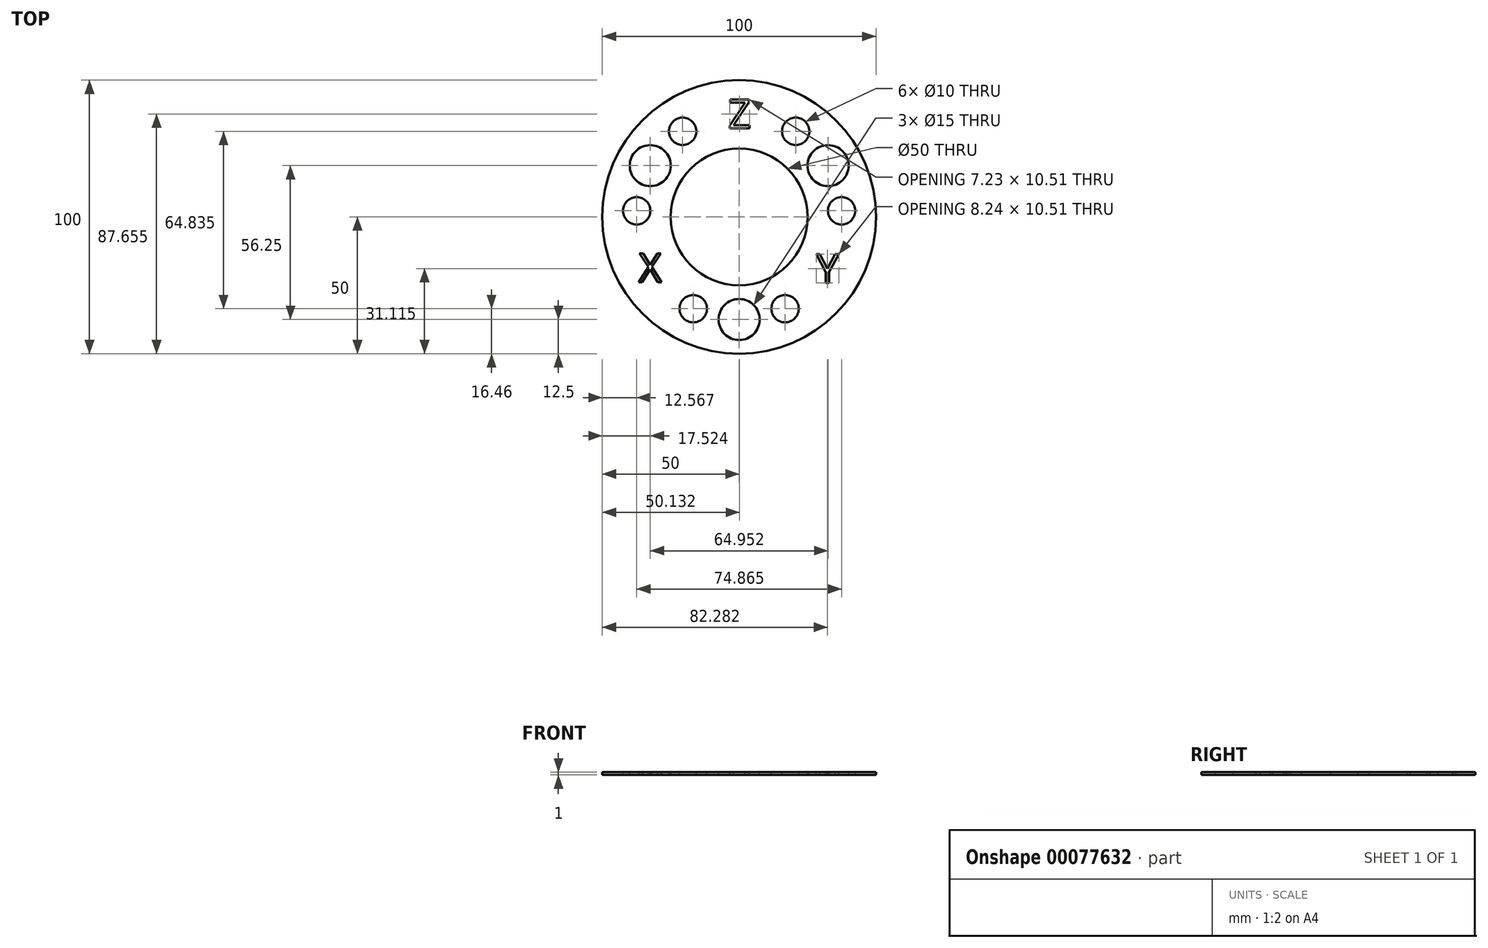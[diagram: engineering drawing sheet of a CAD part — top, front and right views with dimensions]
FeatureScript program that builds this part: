
annotation { "Feature Type Name" : "Feature", "Feature Type Description" : "" }
export const myFeature = defineFeature(function(context is Context, id is Id, definition is map)
    precondition{}
    {
        {
            var Q0;
            Q0=qCreatedBy(makeId("Top.planeOp"),FACE);
            var sketch = newSketch(context, id + "F0", { "sketchPlane" : qUnion([Q0])});
            skCircle(sketch, "E0", {"center": v(0, 0) * mm, "radius": 50 * mm});
            skCircle(sketch, "E1", {"center": v(0, 0) * mm, "radius": 25 * mm});
            skSolve(sketch);
        }
        {
            var Q0;
            Q0 = qSketchRegion(id + "F0", true);
            extrude(context, id + "F1", {"entities" : qUnion([Q0]), "depth" : 1 * mm});
        }
        {
            var Q0;
            Q0=makeQuery(id+"F1.opExtrude","CAP_FACE",FACE,{"disambiguationData":[OSD([sQuery(id+"F0.wireOp",EDGE,"E0"),sQuery(id+"F0.wireOp",EDGE,"E1")])],"isStart":false});
            var sketch = newSketch(context, id + "F2", { "sketchPlane" : qUnion([Q0])});
            skLineSegment(sketch, "E2", {"start": v(0, 0) * mm, "end": v(-32.48, -18.75) * mm, "construction": true});
            skLineSegment(sketch, "E3", {"start": v(32.48, -18.75) * mm, "end": v(0, 0) * mm, "construction": true});
            skLineSegment(sketch, "E4", {"start": v(0, 37.5) * mm, "end": v(0, 0) * mm, "construction": true});
            skCircle(sketch, "E5", {"center": v(0, 0) * mm, "radius": 37.5 * mm, "construction": true});
            skText(sketch, "E6", { "text": "X\n", "fontName": "OpenSans-Regular.ttf"});
            skText(sketch, "E7", { "text": "Y", "fontName": "OpenSans-Regular.ttf"});
            skText(sketch, "E8", { "text": "Z", "fontName": "OpenSans-Regular.ttf"});
            skCircle(sketch, "E9", {"center": v(-32.48, 18.75) * mm, "radius": 7.5 * mm});
            skCircle(sketch, "E10", {"center": v(-20.66, 31.3) * mm, "radius": 5 * mm});
            skCircle(sketch, "E11", {"center": v(-37.43, 2.25) * mm, "radius": 5 * mm});
            skCircle(sketch, "E12.MirrorC", {"center": v(37.43, 2.25) * mm, "radius": 5 * mm});
            skCircle(sketch, "E13.MirrorC", {"center": v(32.48, 18.75) * mm, "radius": 7.5 * mm});
            skCircle(sketch, "E14.MirrorC", {"center": v(20.66, 31.3) * mm, "radius": 5 * mm});
            skCircle(sketch, "E15.MirrorC", {"center": v(16.77, -33.54) * mm, "radius": 5 * mm});
            skCircle(sketch, "E16.MirrorC", {"center": v(0, -37.5) * mm, "radius": 7.5 * mm});
            skCircle(sketch, "E17.MirrorC", {"center": v(-16.77, -33.54) * mm, "radius": 5 * mm});
            const initialGuessF2  = {"E6": [-0.03677, -0.02383, 1, 0, 0.0106], "E7": [0.02816, -0.02414, 1, 0, 0.0106], "E8": [-0.00407, 0.0324, 1, 0, 0.0106]};
            skSetInitialGuess(sketch, initialGuessF2);
            skSolve(sketch);
        }
        {
            var Q0;
            Q0 = qSketchRegion(id + "F2", true);
            extrude(context, id + "F3", {"entities" : qUnion([Q0]), "operationType" : NewBodyOperationType.REMOVE, "endBound" : BoundingType.THROUGH_ALL, "oppositeDirection" : true, "depth" : 25.4 * mm});
        }
    });
